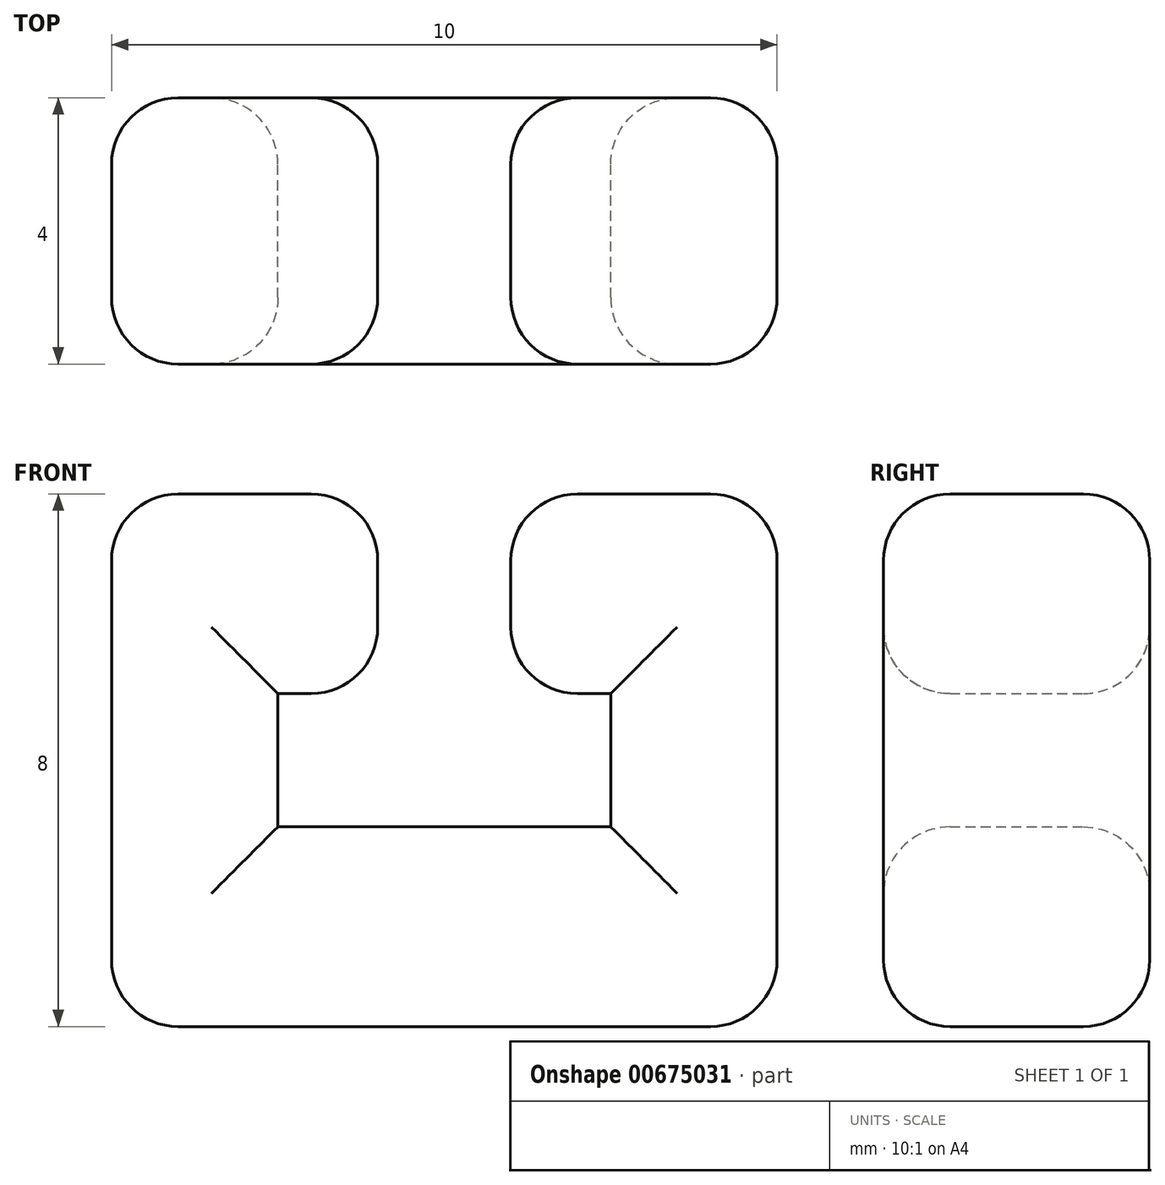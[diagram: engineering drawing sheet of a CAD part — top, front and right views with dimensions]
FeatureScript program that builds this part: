
annotation { "Feature Type Name" : "Feature", "Feature Type Description" : "" }
export const myFeature = defineFeature(function(context is Context, id is Id, definition is map)
    precondition{}
    {
        {
            var Q0;
            Q0=qCreatedBy(makeId("Front.planeOp"),FACE);
            var sketch = newSketch(context, id + "F0", { "sketchPlane" : qUnion([Q0])});
            skLineSegment(sketch, "E0", {"start": v(0, 0) * mm, "end": v(-5, 0) * mm});
            skLineSegment(sketch, "E1", {"start": v(-5, 0) * mm, "end": v(-5, 8) * mm});
            skLineSegment(sketch, "E2", {"start": v(-5, 8) * mm, "end": v(-1, 8) * mm});
            skLineSegment(sketch, "E3", {"start": v(-1, 8) * mm, "end": v(-1, 5) * mm});
            skLineSegment(sketch, "E4", {"start": v(-1, 5) * mm, "end": v(-2.5, 5) * mm});
            skLineSegment(sketch, "E5", {"start": v(-2.5, 5) * mm, "end": v(-2.5, 3) * mm});
            skLineSegment(sketch, "E6", {"start": v(-2.5, 3) * mm, "end": v(0, 3) * mm});
            skLineSegment(sketch, "E7.MirrorCS", {"start": v(0, 0) * mm, "end": v(5, 0) * mm});
            skLineSegment(sketch, "E8.MirrorCS", {"start": v(5, 0) * mm, "end": v(5, 8) * mm});
            skLineSegment(sketch, "E9.MirrorCS", {"start": v(5, 8) * mm, "end": v(1, 8) * mm});
            skLineSegment(sketch, "E10.MirrorCS", {"start": v(1, 8) * mm, "end": v(1, 5) * mm});
            skLineSegment(sketch, "E11.MirrorCS", {"start": v(1, 5) * mm, "end": v(2.5, 5) * mm});
            skLineSegment(sketch, "E12.MirrorCS", {"start": v(2.5, 5) * mm, "end": v(2.5, 3) * mm});
            skLineSegment(sketch, "E13.MirrorCS", {"start": v(2.5, 3) * mm, "end": v(0, 3) * mm});
            skSolve(sketch);
        }
        {
            var Q0;
            Q0=makeQuery(id+"F0.imprint","IMPRINT",FACE,{"disambiguationData":[TD([[makeQuery(id+"F0.imprint","IMPRINT",EDGE,{"derivedFrom":sQuery(id+"F0.wireOp",EDGE,"E0")}),-1.0]])]});
            extrude(context, id + "F1", {"entities" : qUnion([Q0]), "depth" : 4 * mm, "offsetDistance" : 25 * mm});
        }
        {
            var Q0;
            Q0=makeQuery(id+"F1.opExtrude","CAP_EDGE",EDGE,{"disambiguationData":[OSD([sQuery(id+"F0.wireOp",EDGE,"E9.MirrorCS")])],"isStart":false});
            var Q1;
            Q1=makeQuery(id+"F1.opExtrude","CAP_EDGE",EDGE,{"disambiguationData":[OSD([sQuery(id+"F0.wireOp",EDGE,"E8.MirrorCS")])],"isStart":false});
            var Q2;
            Q2=makeQuery(id+"F1.opExtrude","SWEPT_EDGE",EDGE,{"disambiguationData":[OSD([sQuery(id+"F0.wireOp",EDGE,"E8.MirrorCS"),sQuery(id+"F0.wireOp",EDGE,"E9.MirrorCS")])]});
            var Q3;
            Q3=makeQuery(id+"F1.opExtrude","CAP_EDGE",EDGE,{"disambiguationData":[OSD([sQuery(id+"F0.wireOp",EDGE,"E2")])],"isStart":false});
            var Q4;
            Q4=makeQuery(id+"F1.opExtrude","CAP_FACE",FACE,{"disambiguationData":[OSD([sQuery(id+"F0.wireOp",EDGE,"E0"),sQuery(id+"F0.wireOp",EDGE,"E1"),sQuery(id+"F0.wireOp",EDGE,"E2"),sQuery(id+"F0.wireOp",EDGE,"E3"),sQuery(id+"F0.wireOp",EDGE,"E4"),sQuery(id+"F0.wireOp",EDGE,"E5"),sQuery(id+"F0.wireOp",EDGE,"E6"),sQuery(id+"F0.wireOp",EDGE,"E7.MirrorCS"),sQuery(id+"F0.wireOp",EDGE,"E8.MirrorCS"),sQuery(id+"F0.wireOp",EDGE,"E9.MirrorCS"),sQuery(id+"F0.wireOp",EDGE,"E10.MirrorCS"),sQuery(id+"F0.wireOp",EDGE,"E11.MirrorCS"),sQuery(id+"F0.wireOp",EDGE,"E12.MirrorCS"),sQuery(id+"F0.wireOp",EDGE,"E13.MirrorCS")])],"isStart":false});
            var Q5;
            Q5=makeQuery(id+"F1.opExtrude","SWEPT_FACE",FACE,{"disambiguationData":[OSD([sQuery(id+"F0.wireOp",EDGE,"E2")])]});
            var Q6;
            Q6=makeQuery(id+"F1.opExtrude","SWEPT_FACE",FACE,{"disambiguationData":[OSD([sQuery(id+"F0.wireOp",EDGE,"E3")])]});
            var Q7;
            Q7=makeQuery(id+"F1.opExtrude","SWEPT_FACE",FACE,{"disambiguationData":[OSD([sQuery(id+"F0.wireOp",EDGE,"E9.MirrorCS")])]});
            var Q8;
            Q8=makeQuery(id+"F1.opExtrude","SWEPT_FACE",FACE,{"disambiguationData":[OSD([sQuery(id+"F0.wireOp",EDGE,"E8.MirrorCS")])]});
            var Q9;
            Q9=makeQuery(id+"F1.opExtrude","CAP_FACE",FACE,{"disambiguationData":[OSD([sQuery(id+"F0.wireOp",EDGE,"E0"),sQuery(id+"F0.wireOp",EDGE,"E1"),sQuery(id+"F0.wireOp",EDGE,"E2"),sQuery(id+"F0.wireOp",EDGE,"E3"),sQuery(id+"F0.wireOp",EDGE,"E4"),sQuery(id+"F0.wireOp",EDGE,"E5"),sQuery(id+"F0.wireOp",EDGE,"E6"),sQuery(id+"F0.wireOp",EDGE,"E7.MirrorCS"),sQuery(id+"F0.wireOp",EDGE,"E8.MirrorCS"),sQuery(id+"F0.wireOp",EDGE,"E9.MirrorCS"),sQuery(id+"F0.wireOp",EDGE,"E10.MirrorCS"),sQuery(id+"F0.wireOp",EDGE,"E11.MirrorCS"),sQuery(id+"F0.wireOp",EDGE,"E12.MirrorCS"),sQuery(id+"F0.wireOp",EDGE,"E13.MirrorCS")])],"isStart":true});
            var Q10;
            Q10=makeQuery(id+"F1.opExtrude","SWEPT_FACE",FACE,{"disambiguationData":[OSD([sQuery(id+"F0.wireOp",EDGE,"E0"),sQuery(id+"F0.wireOp",EDGE,"E7.MirrorCS")])]});
            var Q11;
            Q11=makeQuery(id+"F1.opExtrude","SWEPT_FACE",FACE,{"disambiguationData":[OSD([sQuery(id+"F0.wireOp",EDGE,"E1")])]});
            fillet(context, id + "F2", {"entities" : qUnion([Q0, Q1, Q2, Q3, Q4, Q5, Q6, Q7, Q8, Q9, Q10, Q11]), "radius" : 1 * mm, "tangentPropagation" : true, "allowEdgeOverflow" : false});
        }
        {
            var Q0;
            Q0=makeQuery(id+"F1.opExtrude","SWEPT_EDGE",EDGE,{"disambiguationData":[OSD([sQuery(id+"F0.wireOp",EDGE,"E10.MirrorCS"),sQuery(id+"F0.wireOp",EDGE,"E11.MirrorCS")])]});
            fillet(context, id + "F3", {"entities" : qUnion([Q0]), "radius" : 1 * mm, "tangentPropagation" : true, "allowEdgeOverflow" : false});
        }
    });
